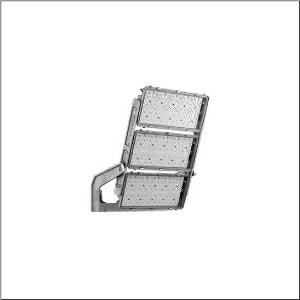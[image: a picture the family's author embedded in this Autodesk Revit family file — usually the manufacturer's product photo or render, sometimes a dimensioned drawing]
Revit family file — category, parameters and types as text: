
# Revit family: floodlight_fl_11_maxi_pro_remote___pl52_5xa779427d01ba_83dd
name_source: partatom
category: Lighting Fixtures
units: mm (PartAtom-declared; Revit-internal decimal feet)

## family parameters
Cut with Voids When Loaded = No
Host = Face
Light Source = No
Part Type = Normal
Room Calculation Point = No
Round Connector Dimension = Use Diameter
Shared = No

## types (1)
- --- (1 x LED, 148130 lm, 1095.9 W, 5000K)
    Apparent Load = 1096 VA
    CIE Flux Codes = 24 55 98 100 100
    Color Rendering = 70
    Color Temperature = 5000K
    Default Elevation = 1800 mm
    Description = Floodlight FL 11  maxi  pro Remote floodlight; light control with lens of PMMA; cover panel of toughened safety glass, transparent; light distribution: PL52, asymmetric direct distribution, LEDcolour temperature: 5000K, rated luminous flux: 148.130lm, colour rendering: CRI > 70, light colour: 750; luminous efficacy: 135lm/W; brightness control: DALI 2 (1 DALI address); with terminal, 8-pole, max. 2.5mm², mains connection: 220..240V/380..400V AC, 50/60Hz, surge voltage resistance: line to ground: 10kV, ECG replaceable separately, LED unit replaceable without ESD environment, dustproof LED module, dimming range 10..100%, no afterglow with DALI off / DMX off command; 1096W floodlight with 3x LED unit of diecast aluminium, coated grey; length: 713mm / width: 651mm / height: 338mm; mounting bracket, of diecast aluminium, uncoated, natural, equipment: Power, protection rating (complete): IP66; insulation class (complete): insulation class I (protective earthing); certification: CE, ENEC, VDE; ball protection: ball impact resistance with accessories, impact resistance: IK07; rated ambient temperature 10°C, only for outdoor installations, permissible operating ambient temperature: -40..+40°C, permissible storage temperature: -40..+85°Cpackaging unit: 1 piece

Light Distribution: PL52
    Height = 320 mm
    Lamp = 1 x LED
    Lamp Light Flux = 148130 lm
    Lamp Power = 1095.9 W
    Lamp count = 1
    Length = 1002 mm
    Luminous efficacy = 135 lm/W
    Manufacturer = Siteco
    ModVariant = No
    Model = 5XA779427D01BA
    Mounting Place = Ceiling
    Mounting Type = Surface mounted
    Number of Poles = 1
    OnlyDefault = Yes
    Power Factor = 1
    Product Name = Floodlight FL 11 maxi pro Remote | PL52
    Product group = floodlight | ceiling mounted
    ProductGroupID = 301
    Protection Class = Protection class I
    Protection Degree = IP 66
    RLX_Detail_Level = 1
    RLX_Emergency_Light_Flux = 0 lm
    RLX_Emergency_Type = 0
    RLX_Emergency_Type_DB = No
    RlxData = <blob elided: 52529 chars, md5=86ad61c1>
    Socket = socket
    Standby Power = 0 W
    System Light Flux = 148130 lm
    System Power = 1096 W
    Type Comments = factory setting: luminous flux: 100 % | dim-lin: 254 | 760 mA
    Type Image = l_1349141.jpg
    URL = http://relux.com
    VarID = @adj_097944
    Voltage = 0 V
    Weight = 0.00 kg
    Width = 655 mm

## geometry (parser evidence)
native form markers: Blend x4, Sweep x14
no freeform markers — native parametric forms only
